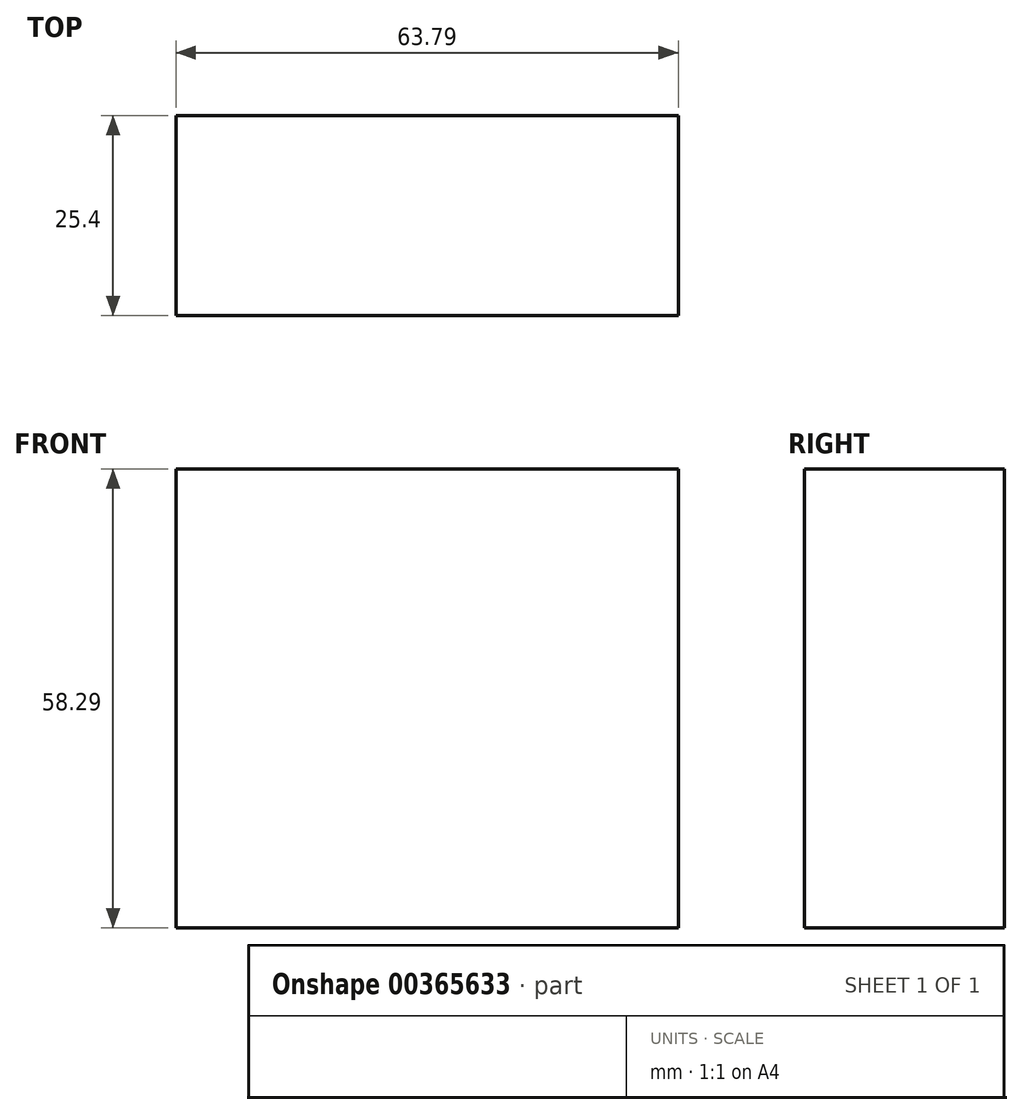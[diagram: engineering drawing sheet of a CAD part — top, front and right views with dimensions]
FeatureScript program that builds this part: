
annotation { "Feature Type Name" : "Feature", "Feature Type Description" : "" }
export const myFeature = defineFeature(function(context is Context, id is Id, definition is map)
    precondition{}
    {
        {
            var Q0;
            Q0=qCreatedBy(makeId("Front.planeOp"),FACE);
            var sketch = newSketch(context, id + "F0", { "sketchPlane" : qUnion([Q0])});
            skLineSegment(sketch, "E0.bottom", {"start": v(0, 0) * mm, "end": v(63.8, 0) * mm});
            skLineSegment(sketch, "E0.top", {"start": v(0, 58.3) * mm, "end": v(63.8, 58.3) * mm});
            skLineSegment(sketch, "E0.left", {"start": v(0, 0) * mm, "end": v(0, 58.3) * mm});
            skLineSegment(sketch, "E0.right", {"start": v(63.8, 0) * mm, "end": v(63.8, 58.3) * mm});
            skSolve(sketch);
        }
        {
            var Q0;
            Q0=makeQuery(id+"F0.imprint","IMPRINT",FACE,{"disambiguationData":[TD([[makeQuery(id+"F0.imprint","IMPRINT",EDGE,{"derivedFrom":sQuery(id+"F0.wireOp",EDGE,"E0.bottom")}),1.0]])]});
            var Q1;
            Q1=makeQuery(id+"F0.imprint","IMPRINT",FACE,{"disambiguationData":[TD([[makeQuery(id+"F0.imprint","IMPRINT",EDGE,{"derivedFrom":sQuery(id+"F0.wireOp",EDGE,"E0.bottom")}),1.0]])]});
            extrude(context, id + "F1", {"entities" : qUnion([Q0, Q1]), "depth" : 25.4 * mm});
        }
    });
